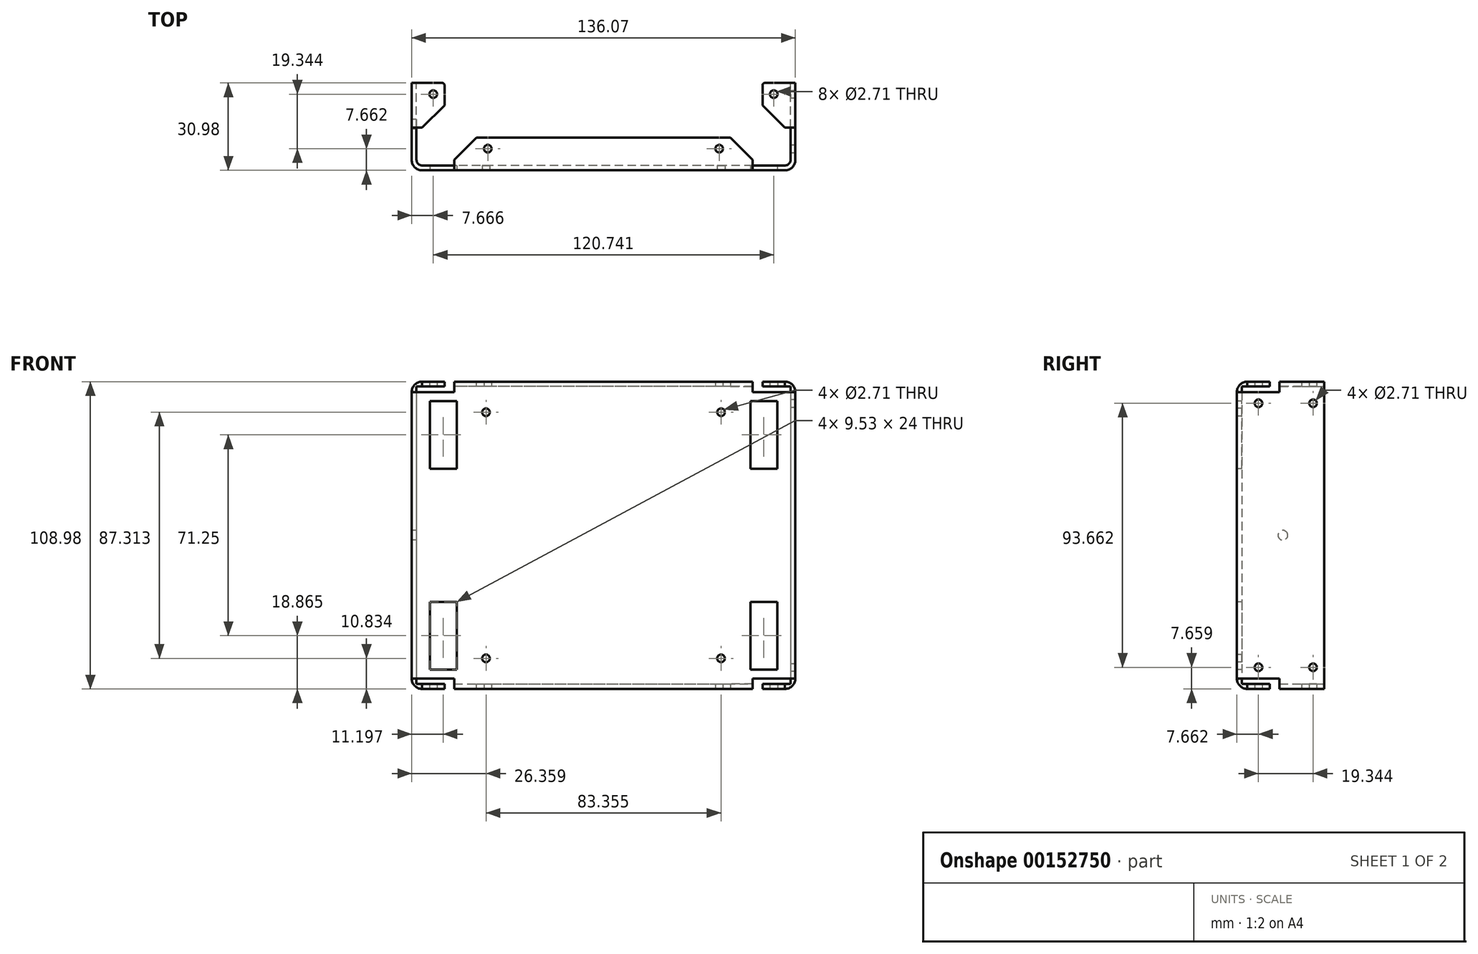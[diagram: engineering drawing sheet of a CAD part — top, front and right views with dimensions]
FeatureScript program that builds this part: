
annotation { "Feature Type Name" : "Feature", "Feature Type Description" : "" }
export const myFeature = defineFeature(function(context is Context, id is Id, definition is map)
    precondition{}
    {
        {
            var Q0;
            Q0=qCreatedBy(makeId("Top.planeOp"),FACE);
            var sketch = newSketch(context, id + "F0", { "sketchPlane" : qUnion([Q0])});
            skLineSegment(sketch, "E0.bottom", {"start": v(0, 0) * mm, "end": v(-132.65, 0) * mm});
            skLineSegment(sketch, "E0.top", {"start": v(1.7, -1.7) * mm, "end": v(-134.36, -1.7) * mm});
            skLineSegment(sketch, "E1.top", {"start": v(-132.65, 29.27) * mm, "end": v(-134.36, 29.27) * mm});
            skLineSegment(sketch, "E1.left", {"start": v(-132.65, 0) * mm, "end": v(-132.65, 29.27) * mm});
            skLineSegment(sketch, "E1.right", {"start": v(-134.36, -1.7) * mm, "end": v(-134.36, 29.27) * mm});
            skLineSegment(sketch, "E2.top", {"start": v(0, 29.27) * mm, "end": v(1.7, 29.27) * mm});
            skLineSegment(sketch, "E2.left", {"start": v(0, 0) * mm, "end": v(0, 29.27) * mm});
            skLineSegment(sketch, "E2.right", {"start": v(1.7, -1.7) * mm, "end": v(1.7, 29.27) * mm});
            skLineSegment(sketch, "E3", {"start": v(-66.32, 0) * mm, "end": v(-66.32, -1.7) * mm, "construction": true});
            skSolve(sketch);
        }
        {
            var Q0;
            Q0=qSketchRegion(id+"F0",true);
            extrude(context, id + "F1", {"entities" : qUnion([Q0]), "depth" : 101.6 * mm});
        }
        {
            var Q0;
            Q0=makeQuery(id+"F1.opExtrude","CAP_FACE",FACE,{"disambiguationData":[OSD([sQuery(id+"F0.wireOp",EDGE,"E0.bottom"),sQuery(id+"F0.wireOp",EDGE,"E0.top"),sQuery(id+"F0.wireOp",EDGE,"E1.top"),sQuery(id+"F0.wireOp",EDGE,"E1.left"),sQuery(id+"F0.wireOp",EDGE,"E1.right"),sQuery(id+"F0.wireOp",EDGE,"E2.top"),sQuery(id+"F0.wireOp",EDGE,"E2.left"),sQuery(id+"F0.wireOp",EDGE,"E2.right")])],"isStart":true});
            var sketch = newSketch(context, id + "F2", { "sketchPlane" : qUnion([Q0])});
            skLineSegment(sketch, "E4.bottom", {"start": v(1.7, -29.27) * mm, "end": v(0, -29.27) * mm});
            skLineSegment(sketch, "E4.top", {"start": v(1.7, -13.4) * mm, "end": v(0, -13.4) * mm});
            skLineSegment(sketch, "E4.left", {"start": v(1.7, -29.27) * mm, "end": v(1.7, -13.4) * mm});
            skLineSegment(sketch, "E4.right", {"start": v(0, -29.27) * mm, "end": v(0, -13.4) * mm});
            skLineSegment(sketch, "E5.bottom", {"start": v(-13.4, 0) * mm, "end": v(-119.26, 0) * mm});
            skLineSegment(sketch, "E5.top", {"start": v(-13.4, 1.7) * mm, "end": v(-119.26, 1.7) * mm});
            skLineSegment(sketch, "E5.left", {"start": v(-13.4, 0) * mm, "end": v(-13.4, 1.7) * mm});
            skLineSegment(sketch, "E5.right", {"start": v(-119.26, 0) * mm, "end": v(-119.26, 1.7) * mm});
            skLineSegment(sketch, "E6.bottom", {"start": v(-132.65, -29.27) * mm, "end": v(-134.36, -29.27) * mm});
            skLineSegment(sketch, "E6.top", {"start": v(-132.65, -13.4) * mm, "end": v(-134.36, -13.4) * mm});
            skLineSegment(sketch, "E6.left", {"start": v(-132.65, -29.27) * mm, "end": v(-132.65, -13.4) * mm});
            skLineSegment(sketch, "E6.right", {"start": v(-134.36, -29.27) * mm, "end": v(-134.36, -13.4) * mm});
            skPoint(sketch, "E7", {"position": v(-66.32, 0) * mm});
            skLineSegment(sketch, "E8.top", {"start": v(-119.26, -13.4) * mm, "end": v(-132.65, -13.4) * mm, "construction": true});
            skLineSegment(sketch, "E8.left", {"start": v(-119.26, 0) * mm, "end": v(-119.26, -13.4) * mm, "construction": true});
            skSolve(sketch);
        }
        {
            var Q0;
            Q0=qSketchRegion(id+"F2",true);
            extrude(context, id + "F3", {"entities" : qUnion([Q0]), "operationType" : NewBodyOperationType.ADD, "depth" : 3.7 * mm});
        }
        {
            var Q0;
            Q0=makeQuery(id+"F1.opExtrude","CAP_FACE",FACE,{"disambiguationData":[OSD([sQuery(id+"F0.wireOp",EDGE,"E0.bottom"),sQuery(id+"F0.wireOp",EDGE,"E0.top"),sQuery(id+"F0.wireOp",EDGE,"E1.top"),sQuery(id+"F0.wireOp",EDGE,"E1.left"),sQuery(id+"F0.wireOp",EDGE,"E1.right"),sQuery(id+"F0.wireOp",EDGE,"E2.top"),sQuery(id+"F0.wireOp",EDGE,"E2.left"),sQuery(id+"F0.wireOp",EDGE,"E2.right")])],"isStart":false});
            var sketch = newSketch(context, id + "F4", { "sketchPlane" : qUnion([Q0])});
            skLineSegment(sketch, "E9.bottom", {"start": v(-134.36, 29.27) * mm, "end": v(-132.65, 29.27) * mm});
            skLineSegment(sketch, "E9.top", {"start": v(-134.36, 13.4) * mm, "end": v(-132.65, 13.4) * mm});
            skLineSegment(sketch, "E9.left", {"start": v(-134.36, 29.27) * mm, "end": v(-134.36, 13.4) * mm});
            skLineSegment(sketch, "E9.right", {"start": v(-132.65, 29.27) * mm, "end": v(-132.65, 13.4) * mm});
            skLineSegment(sketch, "E10.bottom", {"start": v(0, 29.27) * mm, "end": v(1.7, 29.27) * mm});
            skLineSegment(sketch, "E10.top", {"start": v(0, 13.4) * mm, "end": v(1.7, 13.4) * mm});
            skLineSegment(sketch, "E10.left", {"start": v(0, 29.27) * mm, "end": v(0, 13.4) * mm});
            skLineSegment(sketch, "E10.right", {"start": v(1.7, 29.27) * mm, "end": v(1.7, 13.4) * mm});
            skLineSegment(sketch, "E11.bottom", {"start": v(-13.4, -1.7) * mm, "end": v(-119.26, -1.7) * mm});
            skLineSegment(sketch, "E11.top", {"start": v(-13.4, 0) * mm, "end": v(-119.26, 0) * mm});
            skLineSegment(sketch, "E11.left", {"start": v(-13.4, -1.7) * mm, "end": v(-13.4, 0) * mm});
            skLineSegment(sketch, "E11.right", {"start": v(-119.26, -1.7) * mm, "end": v(-119.26, 0) * mm});
            skSolve(sketch);
        }
        {
            var Q0;
            Q0=qSketchRegion(id+"F4",true);
            extrude(context, id + "F5", {"entities" : qUnion([Q0]), "operationType" : NewBodyOperationType.ADD, "depth" : 3.7 * mm});
        }
        {
            var Q0;
            Q0=makeQuery(id+"F5.boolean.opBoolean","MERGE",FACE,{"derivedFrom":[makeQuery(id+"F3.boolean.opBoolean","MERGE",FACE,{"derivedFrom":[makeQuery(id+"F1.opExtrude","SWEPT_FACE",FACE,{"disambiguationData":[OSD([sQuery(id+"F0.wireOp",EDGE,"E0.bottom")])]}),makeQuery(id+"F3.opExtrude","SWEPT_FACE",FACE,{"disambiguationData":[OSD([sQuery(id+"F2.wireOp",EDGE,"E5.bottom")])]})]}),makeQuery(id+"F5.opExtrude","SWEPT_FACE",FACE,{"disambiguationData":[OSD([sQuery(id+"F4.wireOp",EDGE,"E11.top")])]})]});
            var sketch = newSketch(context, id + "F6", { "sketchPlane" : qUnion([Q0])});
            skLineSegment(sketch, "E12.bottom", {"start": v(119.26, -3.7) * mm, "end": v(13.4, -3.7) * mm});
            skLineSegment(sketch, "E12.top", {"start": v(119.26, -1.98) * mm, "end": v(13.4, -1.98) * mm});
            skLineSegment(sketch, "E12.left", {"start": v(119.26, -3.7) * mm, "end": v(119.26, -1.98) * mm});
            skLineSegment(sketch, "E12.right", {"start": v(13.4, -3.7) * mm, "end": v(13.4, -1.98) * mm});
            skLineSegment(sketch, "E13.bottom", {"start": v(13.4, 105.3) * mm, "end": v(119.26, 105.3) * mm});
            skLineSegment(sketch, "E13.top", {"start": v(13.4, 103.58) * mm, "end": v(119.26, 103.58) * mm});
            skLineSegment(sketch, "E13.left", {"start": v(13.4, 105.3) * mm, "end": v(13.4, 103.58) * mm});
            skLineSegment(sketch, "E13.right", {"start": v(119.26, 105.3) * mm, "end": v(119.26, 103.58) * mm});
            skSolve(sketch);
        }
        {
            var Q0;
            Q0=qSketchRegion(id+"F6",true);
            extrude(context, id + "F7", {"entities" : qUnion([Q0]), "operationType" : NewBodyOperationType.ADD, "depth" : 9.92 * mm});
        }
        {
            var Q0;
            Q0=makeQuery(id+"F5.boolean.opBoolean","MERGE",FACE,{"derivedFrom":[makeQuery(id+"F3.boolean.opBoolean","MERGE",FACE,{"derivedFrom":[makeQuery(id+"F1.opExtrude","SWEPT_FACE",FACE,{"disambiguationData":[OSD([sQuery(id+"F0.wireOp",EDGE,"E1.left")])]}),makeQuery(id+"F3.opExtrude","SWEPT_FACE",FACE,{"disambiguationData":[OSD([sQuery(id+"F2.wireOp",EDGE,"E6.left")])]})]}),makeQuery(id+"F5.opExtrude","SWEPT_FACE",FACE,{"disambiguationData":[OSD([sQuery(id+"F4.wireOp",EDGE,"E9.right")])]})]});
            var sketch = newSketch(context, id + "F8", { "sketchPlane" : qUnion([Q0])});
            skLineSegment(sketch, "E14.bottom", {"start": v(13.4, 105.3) * mm, "end": v(29.27, 105.3) * mm});
            skLineSegment(sketch, "E14.top", {"start": v(13.4, 103.58) * mm, "end": v(29.27, 103.58) * mm});
            skLineSegment(sketch, "E14.left", {"start": v(13.4, 105.3) * mm, "end": v(13.4, 103.58) * mm});
            skLineSegment(sketch, "E14.right", {"start": v(29.27, 105.3) * mm, "end": v(29.27, 103.58) * mm});
            skLineSegment(sketch, "E15.bottom", {"start": v(13.4, -3.7) * mm, "end": v(29.27, -3.7) * mm});
            skLineSegment(sketch, "E15.top", {"start": v(13.4, -1.98) * mm, "end": v(29.27, -1.98) * mm});
            skLineSegment(sketch, "E15.left", {"start": v(13.4, -3.7) * mm, "end": v(13.4, -1.98) * mm});
            skLineSegment(sketch, "E15.right", {"start": v(29.27, -3.7) * mm, "end": v(29.27, -1.98) * mm});
            skSolve(sketch);
        }
        {
            var Q0;
            Q0=qSketchRegion(id+"F8",true);
            extrude(context, id + "F9", {"entities" : qUnion([Q0]), "operationType" : NewBodyOperationType.ADD, "depth" : 9.92 * mm});
        }
        {
            var Q0;
            Q0=makeQuery(id+"F5.boolean.opBoolean","MERGE",FACE,{"derivedFrom":[makeQuery(id+"F3.boolean.opBoolean","MERGE",FACE,{"derivedFrom":[makeQuery(id+"F1.opExtrude","SWEPT_FACE",FACE,{"disambiguationData":[OSD([sQuery(id+"F0.wireOp",EDGE,"E2.left")])]}),makeQuery(id+"F3.opExtrude","SWEPT_FACE",FACE,{"disambiguationData":[OSD([sQuery(id+"F2.wireOp",EDGE,"E4.right")])]})]}),makeQuery(id+"F5.opExtrude","SWEPT_FACE",FACE,{"disambiguationData":[OSD([sQuery(id+"F4.wireOp",EDGE,"E10.left")])]})]});
            var sketch = newSketch(context, id + "F10", { "sketchPlane" : qUnion([Q0])});
            skLineSegment(sketch, "E16.bottom", {"start": v(-13.4, -3.7) * mm, "end": v(-29.27, -3.7) * mm});
            skLineSegment(sketch, "E16.top", {"start": v(-13.4, -1.98) * mm, "end": v(-29.27, -1.98) * mm});
            skLineSegment(sketch, "E16.left", {"start": v(-13.4, -3.7) * mm, "end": v(-13.4, -1.98) * mm});
            skLineSegment(sketch, "E16.right", {"start": v(-29.27, -3.7) * mm, "end": v(-29.27, -1.98) * mm});
            skLineSegment(sketch, "E17.bottom", {"start": v(-13.4, 105.3) * mm, "end": v(-29.27, 105.3) * mm});
            skLineSegment(sketch, "E17.top", {"start": v(-13.4, 103.58) * mm, "end": v(-29.27, 103.58) * mm});
            skLineSegment(sketch, "E17.left", {"start": v(-13.4, 105.3) * mm, "end": v(-13.4, 103.58) * mm});
            skLineSegment(sketch, "E17.right", {"start": v(-29.27, 105.3) * mm, "end": v(-29.27, 103.58) * mm});
            skSolve(sketch);
        }
        {
            var Q0;
            Q0=qSketchRegion(id+"F10",true);
            extrude(context, id + "F11", {"entities" : qUnion([Q0]), "operationType" : NewBodyOperationType.ADD, "depth" : 9.92 * mm});
        }
        {
            var Q0;
            Q0=makeQuery(id+"F11.opExtrude","CAP_EDGE",EDGE,{"disambiguationData":[OSD([sQuery(id+"F10.wireOp",EDGE,"E17.top")])],"isStart":true});
            var Q1;
            Q1=makeQuery(id+"F7.opExtrude","CAP_EDGE",EDGE,{"disambiguationData":[OSD([sQuery(id+"F6.wireOp",EDGE,"E13.top")])],"isStart":true});
            var Q2;
            Q2=makeQuery(id+"F9.opExtrude","CAP_EDGE",EDGE,{"disambiguationData":[OSD([sQuery(id+"F8.wireOp",EDGE,"E14.top")])],"isStart":true});
            var Q3;
            Q3=makeQuery(id+"F9.opExtrude","CAP_EDGE",EDGE,{"disambiguationData":[OSD([sQuery(id+"F8.wireOp",EDGE,"E15.top")])],"isStart":true});
            var Q4;
            Q4=makeQuery(id+"F7.opExtrude","CAP_EDGE",EDGE,{"disambiguationData":[OSD([sQuery(id+"F6.wireOp",EDGE,"E12.top")])],"isStart":true});
            var Q5;
            Q5=makeQuery(id+"F11.opExtrude","CAP_EDGE",EDGE,{"disambiguationData":[OSD([sQuery(id+"F10.wireOp",EDGE,"E16.top")])],"isStart":true});
            var Q6;
            Q6=makeQuery(id+"F1.opExtrude","SWEPT_EDGE",EDGE,{"disambiguationData":[OSD([sQuery(id+"F0.wireOp",EDGE,"E0.bottom"),sQuery(id+"F0.wireOp",EDGE,"E2.left")])]});
            var Q7;
            Q7=makeQuery(id+"F1.opExtrude","SWEPT_EDGE",EDGE,{"disambiguationData":[OSD([sQuery(id+"F0.wireOp",EDGE,"E0.bottom"),sQuery(id+"F0.wireOp",EDGE,"E1.left")])]});
            fillet(context, id + "F12", {"entities" : qUnion([Q0, Q1, Q2, Q3, Q4, Q5, Q6, Q7]), "radius" : 1.98 * mm, "tangentPropagation" : true, "allowEdgeOverflow" : false});
        }
        {
            var Q0;
            Q0=makeQuery(id+"F3.opExtrude","CAP_EDGE",EDGE,{"disambiguationData":[OSD([sQuery(id+"F2.wireOp",EDGE,"E6.right")])],"isStart":false});
            var Q1;
            Q1=makeQuery(id+"F3.opExtrude","CAP_EDGE",EDGE,{"disambiguationData":[OSD([sQuery(id+"F2.wireOp",EDGE,"E5.top")])],"isStart":false});
            var Q2;
            Q2=makeQuery(id+"F1.opExtrude","SWEPT_EDGE",EDGE,{"disambiguationData":[OSD([sQuery(id+"F0.wireOp",EDGE,"E0.top"),sQuery(id+"F0.wireOp",EDGE,"E1.right")])]});
            var Q3;
            Q3=makeQuery(id+"F5.opExtrude","CAP_EDGE",EDGE,{"disambiguationData":[OSD([sQuery(id+"F4.wireOp",EDGE,"E11.bottom")])],"isStart":false});
            var Q4;
            Q4=makeQuery(id+"F5.opExtrude","CAP_EDGE",EDGE,{"disambiguationData":[OSD([sQuery(id+"F4.wireOp",EDGE,"E9.left")])],"isStart":false});
            var Q5;
            Q5=makeQuery(id+"F3.opExtrude","CAP_EDGE",EDGE,{"disambiguationData":[OSD([sQuery(id+"F2.wireOp",EDGE,"E4.left")])],"isStart":false});
            var Q6;
            Q6=makeQuery(id+"F1.opExtrude","SWEPT_EDGE",EDGE,{"disambiguationData":[OSD([sQuery(id+"F0.wireOp",EDGE,"E0.top"),sQuery(id+"F0.wireOp",EDGE,"E2.right")])]});
            var Q7;
            Q7=makeQuery(id+"F5.opExtrude","CAP_EDGE",EDGE,{"disambiguationData":[OSD([sQuery(id+"F4.wireOp",EDGE,"E10.right")])],"isStart":false});
            fillet(context, id + "F13", {"entities" : qUnion([Q0, Q1, Q2, Q3, Q4, Q5, Q6, Q7]), "radius" : 3.7 * mm, "tangentPropagation" : true, "allowEdgeOverflow" : false});
        }
        {
            var Q0;
            Q0=makeQuery(id+"F9.opExtrude","CAP_EDGE",EDGE,{"disambiguationData":[OSD([sQuery(id+"F8.wireOp",EDGE,"E14.left")])],"isStart":false});
            var Q1;
            Q1=makeQuery(id+"F7.opExtrude","CAP_EDGE",EDGE,{"disambiguationData":[OSD([sQuery(id+"F6.wireOp",EDGE,"E13.right")])],"isStart":false});
            var Q2;
            Q2=makeQuery(id+"F7.opExtrude","CAP_EDGE",EDGE,{"disambiguationData":[OSD([sQuery(id+"F6.wireOp",EDGE,"E13.left")])],"isStart":false});
            var Q3;
            Q3=makeQuery(id+"F11.opExtrude","CAP_EDGE",EDGE,{"disambiguationData":[OSD([sQuery(id+"F10.wireOp",EDGE,"E17.left")])],"isStart":false});
            var Q4;
            Q4=makeQuery(id+"F7.opExtrude","CAP_EDGE",EDGE,{"disambiguationData":[OSD([sQuery(id+"F6.wireOp",EDGE,"E12.right")])],"isStart":false});
            var Q5;
            Q5=makeQuery(id+"F11.opExtrude","CAP_EDGE",EDGE,{"disambiguationData":[OSD([sQuery(id+"F10.wireOp",EDGE,"E16.left")])],"isStart":false});
            var Q6;
            Q6=makeQuery(id+"F9.opExtrude","CAP_EDGE",EDGE,{"disambiguationData":[OSD([sQuery(id+"F8.wireOp",EDGE,"E15.left")])],"isStart":false});
            var Q7;
            Q7=makeQuery(id+"F7.opExtrude","CAP_EDGE",EDGE,{"disambiguationData":[OSD([sQuery(id+"F6.wireOp",EDGE,"E12.left")])],"isStart":false});
            chamfer(context, id + "F14", {"entities" : qUnion([Q0, Q1, Q2, Q3, Q4, Q5, Q6, Q7]), "width" : 7.94 * mm, "tangentPropagation" : true});
        }
        {
            var Q0;
            Q0=makeQuery(id+"F7.boolean.opBoolean","MERGE",FACE,{"derivedFrom":[makeQuery(id+"F3.opExtrude","CAP_FACE",FACE,{"disambiguationData":[OSD([sQuery(id+"F2.wireOp",EDGE,"E5.bottom"),sQuery(id+"F2.wireOp",EDGE,"E5.top"),sQuery(id+"F2.wireOp",EDGE,"E5.left"),sQuery(id+"F2.wireOp",EDGE,"E5.right")])],"isStart":false}),makeQuery(id+"F7.opExtrude","SWEPT_FACE",FACE,{"disambiguationData":[OSD([sQuery(id+"F6.wireOp",EDGE,"E12.bottom")])]})]});
            var sketch = newSketch(context, id + "F15", { "sketchPlane" : qUnion([Q0])});
            skLineSegment(sketch, "E18", {"start": v(-17.36, -5.95) * mm, "end": v(-25.3, -5.95) * mm, "construction": true});
            skLineSegment(sketch, "E19", {"start": v(-25.3, -5.95) * mm, "end": v(-66.32, -5.95) * mm, "construction": true});
            skLineSegment(sketch, "E20", {"start": v(-66.32, -5.95) * mm, "end": v(-107.35, -5.95) * mm, "construction": true});
            skLineSegment(sketch, "E21", {"start": v(-115.29, -5.95) * mm, "end": v(-107.35, -5.95) * mm, "construction": true});
            skCircle(sketch, "E22", {"center": v(-25.3, -5.95) * mm, "radius": 1.35 * mm});
            skCircle(sketch, "E23", {"center": v(-66.32, -5.95) * mm, "radius": 1.35 * mm, "construction": true});
            skCircle(sketch, "E24", {"center": v(-107.35, -5.95) * mm, "radius": 1.35 * mm});
            skLineSegment(sketch, "E25", {"start": v(-5.95, -17.36) * mm, "end": v(-5.95, -25.3) * mm, "construction": true});
            skLineSegment(sketch, "E26", {"start": v(-126.7, -17.36) * mm, "end": v(-126.7, -25.3) * mm, "construction": true});
            skCircle(sketch, "E27", {"center": v(-126.7, -25.3) * mm, "radius": 1.35 * mm});
            skCircle(sketch, "E28", {"center": v(-5.95, -25.3) * mm, "radius": 1.35 * mm});
            skSolve(sketch);
        }
        {
            var Q0;
            Q0=qSketchRegion(id+"F15",true);
            var Q1;
            Q1=makeQuery(id+"F7.boolean.opBoolean","MERGE",FACE,{"derivedFrom":[makeQuery(id+"F5.opExtrude","CAP_FACE",FACE,{"disambiguationData":[OSD([sQuery(id+"F4.wireOp",EDGE,"E11.bottom"),sQuery(id+"F4.wireOp",EDGE,"E11.top"),sQuery(id+"F4.wireOp",EDGE,"E11.left"),sQuery(id+"F4.wireOp",EDGE,"E11.right")])],"isStart":false}),makeQuery(id+"F7.opExtrude","SWEPT_FACE",FACE,{"disambiguationData":[OSD([sQuery(id+"F6.wireOp",EDGE,"E13.bottom")])]})]});
            extrude(context, id + "F16", {"entities" : qUnion([Q0]), "operationType" : NewBodyOperationType.REMOVE, "endBound" : BoundingType.UP_TO_SURFACE, "oppositeDirection" : true, "endBoundEntityFace" : qUnion([Q1]), "depth" : 25.4 * mm});
        }
        {
            var Q0;
            Q0=makeQuery(id+"F9.opExtrude","CAP_EDGE",EDGE,{"disambiguationData":[OSD([sQuery(id+"F8.wireOp",EDGE,"E15.right")])],"isStart":false});
            var Q1;
            Q1=makeQuery(id+"F9.opExtrude","CAP_EDGE",EDGE,{"disambiguationData":[OSD([sQuery(id+"F8.wireOp",EDGE,"E14.right")])],"isStart":false});
            var Q2;
            Q2=makeQuery(id+"F11.opExtrude","CAP_EDGE",EDGE,{"disambiguationData":[OSD([sQuery(id+"F10.wireOp",EDGE,"E17.right")])],"isStart":false});
            var Q3;
            Q3=makeQuery(id+"F11.opExtrude","CAP_EDGE",EDGE,{"disambiguationData":[OSD([sQuery(id+"F10.wireOp",EDGE,"E16.right")])],"isStart":false});
            fillet(context, id + "F17", {"entities" : qUnion([Q0, Q1, Q2, Q3]), "radius" : 0.76 * mm, "tangentPropagation" : true, "allowEdgeOverflow" : false});
        }
        {
            var Q0;
            Q0=makeQuery(id+"F5.boolean.opBoolean","MERGE",FACE,{"derivedFrom":[makeQuery(id+"F3.boolean.opBoolean","MERGE",FACE,{"derivedFrom":[makeQuery(id+"F1.opExtrude","SWEPT_FACE",FACE,{"disambiguationData":[OSD([sQuery(id+"F0.wireOp",EDGE,"E2.right")])]}),makeQuery(id+"F3.opExtrude","SWEPT_FACE",FACE,{"disambiguationData":[OSD([sQuery(id+"F2.wireOp",EDGE,"E4.left")])]})]}),makeQuery(id+"F5.opExtrude","SWEPT_FACE",FACE,{"disambiguationData":[OSD([sQuery(id+"F4.wireOp",EDGE,"E10.right")])]})]});
            var sketch = newSketch(context, id + "F18", { "sketchPlane" : qUnion([Q0])});
            skLineSegment(sketch, "E29.bottom", {"start": v(29.27, 101.6) * mm, "end": v(25.3, 101.6) * mm, "construction": true});
            skLineSegment(sketch, "E29.top", {"start": v(29.27, 97.63) * mm, "end": v(25.3, 97.63) * mm, "construction": true});
            skLineSegment(sketch, "E29.left", {"start": v(29.27, 101.6) * mm, "end": v(29.27, 97.63) * mm, "construction": true});
            skLineSegment(sketch, "E29.right", {"start": v(25.3, 101.6) * mm, "end": v(25.3, 97.63) * mm, "construction": true});
            skLineSegment(sketch, "E30", {"start": v(29.27, 50.8) * mm, "end": v(1.98, 50.8) * mm, "construction": true});
            skLineSegment(sketch, "E31.bottom", {"start": v(25.3, 97.63) * mm, "end": v(5.95, 97.63) * mm, "construction": true});
            skLineSegment(sketch, "E31.top", {"start": v(25.3, 3.97) * mm, "end": v(5.95, 3.97) * mm, "construction": true});
            skLineSegment(sketch, "E31.left", {"start": v(25.3, 97.63) * mm, "end": v(25.3, 3.97) * mm, "construction": true});
            skLineSegment(sketch, "E31.right", {"start": v(5.95, 97.63) * mm, "end": v(5.95, 3.97) * mm, "construction": true});
            skPoint(sketch, "E31.middle", {"position": v(15.62, 50.8) * mm});
            skCircle(sketch, "E32", {"center": v(25.3, 97.63) * mm, "radius": 1.35 * mm});
            skCircle(sketch, "E33", {"center": v(25.3, 3.97) * mm, "radius": 1.35 * mm});
            skCircle(sketch, "E34", {"center": v(5.95, 3.97) * mm, "radius": 1.35 * mm});
            skCircle(sketch, "E35", {"center": v(5.95, 97.63) * mm, "radius": 1.35 * mm});
            skSolve(sketch);
        }
        {
            var Q0;
            Q0 = qSketchRegion(id + "F18", true);
            var Q1;
            Q1=makeQuery(id+"F5.boolean.opBoolean","MERGE",FACE,{"derivedFrom":[makeQuery(id+"F3.boolean.opBoolean","MERGE",FACE,{"derivedFrom":[makeQuery(id+"F1.opExtrude","SWEPT_FACE",FACE,{"disambiguationData":[OSD([sQuery(id+"F0.wireOp",EDGE,"E2.left")])]}),makeQuery(id+"F3.opExtrude","SWEPT_FACE",FACE,{"disambiguationData":[OSD([sQuery(id+"F2.wireOp",EDGE,"E4.right")])]})]}),makeQuery(id+"F5.opExtrude","SWEPT_FACE",FACE,{"disambiguationData":[OSD([sQuery(id+"F4.wireOp",EDGE,"E10.left")])]})]});
            extrude(context, id + "F19", {"entities" : qUnion([Q0]), "operationType" : NewBodyOperationType.REMOVE, "endBound" : BoundingType.UP_TO_SURFACE, "oppositeDirection" : true, "endBoundEntityFace" : qUnion([Q1]), "depth" : 25.4 * mm});
        }
        {
            var Q0;
            Q0=makeQuery(id+"F5.boolean.opBoolean","MERGE",FACE,{"derivedFrom":[makeQuery(id+"F3.boolean.opBoolean","MERGE",FACE,{"derivedFrom":[makeQuery(id+"F1.opExtrude","SWEPT_FACE",FACE,{"disambiguationData":[OSD([sQuery(id+"F0.wireOp",EDGE,"E0.top")])]}),makeQuery(id+"F3.opExtrude","SWEPT_FACE",FACE,{"disambiguationData":[OSD([sQuery(id+"F2.wireOp",EDGE,"E5.top")])]})]}),makeQuery(id+"F5.opExtrude","SWEPT_FACE",FACE,{"disambiguationData":[OSD([sQuery(id+"F4.wireOp",EDGE,"E11.bottom")])]})]});
            var sketch = newSketch(context, id + "F20", { "sketchPlane" : qUnion([Q0])});
            skLineSegment(sketch, "E36.bottom", {"start": v(-4.72, 3.18) * mm, "end": v(-14.25, 3.18) * mm});
            skLineSegment(sketch, "E36.top", {"start": v(-4.72, 27.18) * mm, "end": v(-14.25, 27.18) * mm});
            skLineSegment(sketch, "E36.left", {"start": v(-4.72, 3.18) * mm, "end": v(-4.72, 27.18) * mm});
            skLineSegment(sketch, "E36.right", {"start": v(-14.25, 3.18) * mm, "end": v(-14.25, 27.18) * mm});
            skLineSegment(sketch, "E37.bottom", {"start": v(-127.93, 3.18) * mm, "end": v(-118.4, 3.18) * mm});
            skLineSegment(sketch, "E37.top", {"start": v(-127.93, 27.18) * mm, "end": v(-118.4, 27.18) * mm});
            skLineSegment(sketch, "E37.left", {"start": v(-127.93, 3.18) * mm, "end": v(-127.93, 27.18) * mm});
            skLineSegment(sketch, "E37.right", {"start": v(-118.4, 3.18) * mm, "end": v(-118.4, 27.18) * mm});
            skLineSegment(sketch, "E38.bottom", {"start": v(-127.93, 98.43) * mm, "end": v(-118.4, 98.43) * mm});
            skLineSegment(sketch, "E38.top", {"start": v(-127.93, 74.42) * mm, "end": v(-118.4, 74.42) * mm});
            skLineSegment(sketch, "E38.left", {"start": v(-127.93, 98.43) * mm, "end": v(-127.93, 74.43) * mm});
            skLineSegment(sketch, "E38.right", {"start": v(-118.4, 98.43) * mm, "end": v(-118.4, 74.43) * mm});
            skLineSegment(sketch, "E39.bottom", {"start": v(-4.72, 98.43) * mm, "end": v(-14.25, 98.43) * mm});
            skLineSegment(sketch, "E39.top", {"start": v(-4.72, 74.42) * mm, "end": v(-14.25, 74.42) * mm});
            skLineSegment(sketch, "E39.left", {"start": v(-4.72, 98.43) * mm, "end": v(-4.72, 74.43) * mm});
            skLineSegment(sketch, "E39.right", {"start": v(-14.25, 98.43) * mm, "end": v(-14.25, 74.43) * mm});
            skLineSegment(sketch, "E40", {"start": v(-66.32, 0) * mm, "end": v(-66.32, 101.6) * mm, "construction": true});
            skLineSegment(sketch, "E41.bottom", {"start": v(-14.25, 27.18) * mm, "end": v(-118.4, 27.18) * mm, "construction": true});
            skLineSegment(sketch, "E41.top", {"start": v(-14.25, 74.42) * mm, "end": v(-118.4, 74.42) * mm, "construction": true});
            skLineSegment(sketch, "E41.left", {"start": v(-14.25, 27.18) * mm, "end": v(-14.25, 74.43) * mm, "construction": true});
            skLineSegment(sketch, "E41.right", {"start": v(-118.4, 27.18) * mm, "end": v(-118.4, 74.43) * mm, "construction": true});
            skPoint(sketch, "E41.middle", {"position": v(-66.32, 50.8) * mm});
            skLineSegment(sketch, "E42", {"start": v(-9.48, 27.18) * mm, "end": v(-9.48, 50.8) * mm, "construction": true});
            skLineSegment(sketch, "E43", {"start": v(-9.48, 50.8) * mm, "end": v(-1.98, 50.8) * mm, "construction": true});
            skLineSegment(sketch, "E44", {"start": v(-9.48, 3.18) * mm, "end": v(-9.48, 0) * mm, "construction": true});
            skLineSegment(sketch, "E45.bottom", {"start": v(-24.65, 7.14) * mm, "end": v(-108, 7.14) * mm, "construction": true});
            skLineSegment(sketch, "E45.top", {"start": v(-24.65, 94.46) * mm, "end": v(-108, 94.46) * mm, "construction": true});
            skLineSegment(sketch, "E45.left", {"start": v(-24.65, 7.14) * mm, "end": v(-24.65, 94.46) * mm, "construction": true});
            skLineSegment(sketch, "E45.right", {"start": v(-108, 7.14) * mm, "end": v(-108, 94.46) * mm, "construction": true});
            skLineSegment(sketch, "E46", {"start": v(-24.65, 7.14) * mm, "end": v(-24.65, 3.18) * mm, "construction": true});
            skLineSegment(sketch, "E47", {"start": v(-24.65, 3.18) * mm, "end": v(-14.25, 3.18) * mm, "construction": true});
            skCircle(sketch, "E48", {"center": v(-24.65, 7.14) * mm, "radius": 1.35 * mm});
            skCircle(sketch, "E49", {"center": v(-108, 7.14) * mm, "radius": 1.35 * mm});
            skCircle(sketch, "E50", {"center": v(-108, 94.46) * mm, "radius": 1.35 * mm});
            skCircle(sketch, "E51", {"center": v(-24.65, 94.46) * mm, "radius": 1.35 * mm});
            skPoint(sketch, "E52", {"position": v(-123.16, 3.18) * mm});
            skSolve(sketch);
        }
        {
            var Q0;
            Q0 = qSketchRegion(id + "F20", true);
            var Q1;
            Q1=makeQuery(id+"F5.boolean.opBoolean","MERGE",FACE,{"derivedFrom":[makeQuery(id+"F3.boolean.opBoolean","MERGE",FACE,{"derivedFrom":[makeQuery(id+"F1.opExtrude","SWEPT_FACE",FACE,{"disambiguationData":[OSD([sQuery(id+"F0.wireOp",EDGE,"E0.bottom")])]}),makeQuery(id+"F3.opExtrude","SWEPT_FACE",FACE,{"disambiguationData":[OSD([sQuery(id+"F2.wireOp",EDGE,"E5.bottom")])]})]}),makeQuery(id+"F5.opExtrude","SWEPT_FACE",FACE,{"disambiguationData":[OSD([sQuery(id+"F4.wireOp",EDGE,"E11.top")])]})]});
            extrude(context, id + "F21", {"entities" : qUnion([Q0]), "operationType" : NewBodyOperationType.REMOVE, "endBound" : BoundingType.UP_TO_SURFACE, "oppositeDirection" : true, "endBoundEntityFace" : qUnion([Q1]), "depth" : 25.4 * mm});
        }
        {
            var Q0;
            Q0=makeQuery(id+"F5.boolean.opBoolean","MERGE",FACE,{"derivedFrom":[makeQuery(id+"F3.boolean.opBoolean","MERGE",FACE,{"derivedFrom":[makeQuery(id+"F1.opExtrude","SWEPT_FACE",FACE,{"disambiguationData":[OSD([sQuery(id+"F0.wireOp",EDGE,"E1.right")])]}),makeQuery(id+"F3.opExtrude","SWEPT_FACE",FACE,{"disambiguationData":[OSD([sQuery(id+"F2.wireOp",EDGE,"E6.right")])]})]}),makeQuery(id+"F5.opExtrude","SWEPT_FACE",FACE,{"disambiguationData":[OSD([sQuery(id+"F4.wireOp",EDGE,"E9.left")])]})]});
            var sketch = newSketch(context, id + "F22", { "sketchPlane" : qUnion([Q0])});
            skLineSegment(sketch, "E53", {"start": v(-29.27, 50.8) * mm, "end": v(-14.63, 50.8) * mm, "construction": true});
            skCircle(sketch, "E54", {"center": v(-14.63, 50.8) * mm, "radius": 1.73 * mm});
            skSolve(sketch);
        }
        {
            var Q0;
            Q0 = qSketchRegion(id + "F22", true);
            var Q1;
            Q1=makeQuery(id+"F5.boolean.opBoolean","MERGE",FACE,{"derivedFrom":[makeQuery(id+"F3.boolean.opBoolean","MERGE",FACE,{"derivedFrom":[makeQuery(id+"F1.opExtrude","SWEPT_FACE",FACE,{"disambiguationData":[OSD([sQuery(id+"F0.wireOp",EDGE,"E1.left")])]}),makeQuery(id+"F3.opExtrude","SWEPT_FACE",FACE,{"disambiguationData":[OSD([sQuery(id+"F2.wireOp",EDGE,"E6.left")])]})]}),makeQuery(id+"F5.opExtrude","SWEPT_FACE",FACE,{"disambiguationData":[OSD([sQuery(id+"F4.wireOp",EDGE,"E9.right")])]})]});
            extrude(context, id + "F23", {"entities" : qUnion([Q0]), "operationType" : NewBodyOperationType.REMOVE, "endBound" : BoundingType.UP_TO_SURFACE, "oppositeDirection" : true, "endBoundEntityFace" : qUnion([Q1]), "depth" : 25.4 * mm});
        }
    });
